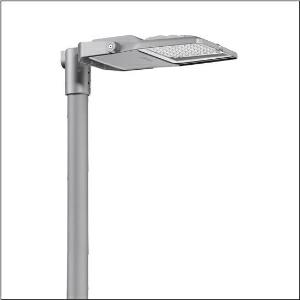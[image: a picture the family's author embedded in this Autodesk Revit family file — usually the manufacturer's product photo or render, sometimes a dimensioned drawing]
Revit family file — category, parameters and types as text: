
# Revit family: floodlight_fl_21_iq_mini___pl33t_5xa7771c2f3a_7d89
name_source: partatom
category: Lighting Fixtures
units: mm (PartAtom-declared; Revit-internal decimal feet)

## family parameters
Cut with Voids When Loaded = No
Host = Face
Light Source = No
Part Type = Normal
Room Calculation Point = No
Round Connector Dimension = Use Diameter
Shared = No

## types (1)
- --- (1 x LED, 12060 lm, 87.2 W, 3000K)
    Apparent Load = 87 VA
    CIE Flux Codes = 26 75 99 100 100
    Color Rendering = 70
    Color Temperature = 3000K
    Default Elevation = 1800 mm
    Description = Floodlight FL 21 iQ mini, floodlight, primary light control with lens, of PMMA, primary optical cover: protective disc, of toughened safety glass, transparent, light distribution: PL33T, light emission: direct distribution, installation type: surface-mounted, LED, High Power LED, rated luminous flux: 12.060lm, luminous efficacy: 138lm/W, light colour: 730, colour temperature: 3000K, control: Auto-Match, Temp-Guard, Lumen-Switch, Night-Set, Smart-Wire, Light-Fading, Desk-Remote (wireless, voltage-free reading and setting of iQ features in the workshop via application-optimized NFC function/RFID function), optimised constant luminous flux control (CLO 2.0), with terminal, 6-pole, mains connection: 220..240V, AC, 50/60Hz, start of lifetime: 87W, end of service life: 92W, reduction: 40W, luminaire housing, of diecast aluminium, powder-coated, Siteco® metallic grey (DB 702S), corrosivity category C5 mid according to DIN EN ISO 12944, sealing non-destructively replaceable, please order mast flange separately, mast bracket, of steel, galvanised, powder-coated, Siteco® metallic grey (DB 702S), protection rating (complete): IP66, insulation class (complete): insulation class II (safety insulation), certification: CE, ENEC, VDE, protection symbol: D, impact resistance: IK08, permissible operating ambient temperature: -40..+40°C, permissible operating ambient temperature for outdoor applications: -40..+50°C, standard: DIN EN 12944, LABS conformity tested according to VDMA 24364:2018-05, packaging unit: 1 piece

Light Distribution: PL33T
    Height = 70 mm
    Lamp = 1 x LED
    Lamp Light Flux = 12060 lm
    Lamp Power = 87.2 W
    Lamp count = 1
    Length = 485 mm
    Luminous efficacy = 138 lm/W
    Manufacturer = Siteco
    ModVariant = No
    Model = 5XA7771C2F3A
    Number of Poles = 1
    OnlyDefault = Yes
    Power Factor = 1
    Product Name = Floodlight FL 21 iQ mini | PL33T
    Product group = floodlight | pylon annexe
    ProductGroupID = 6200
    Protection Class = Protection class II
    Protection Degree = IP 66
    RLX_Detail_Level = 1
    RLX_Emergency_Light_Flux = 0 lm
    RLX_Emergency_Type = 0
    RLX_Emergency_Type_DB = No
    RlxData = <blob elided: 101321 chars, md5=defc5be5>
    Socket = socket
    Standby Power = 0 W
    System Light Flux = 12060 lm
    System Power = 87 W
    Type Comments = factory setting: luminous flux: 100 % | dim-lin: 254 | 456 mA
    Type Image = l_1007125.jpg
    URL = http://relux.com
    VarID = @adj_120077
    Voltage = 0 V
    Weight = 0.00 kg
    Width = 337 mm

## geometry (parser evidence)
native form markers: Blend x4, Sweep x11
no freeform markers — native parametric forms only
